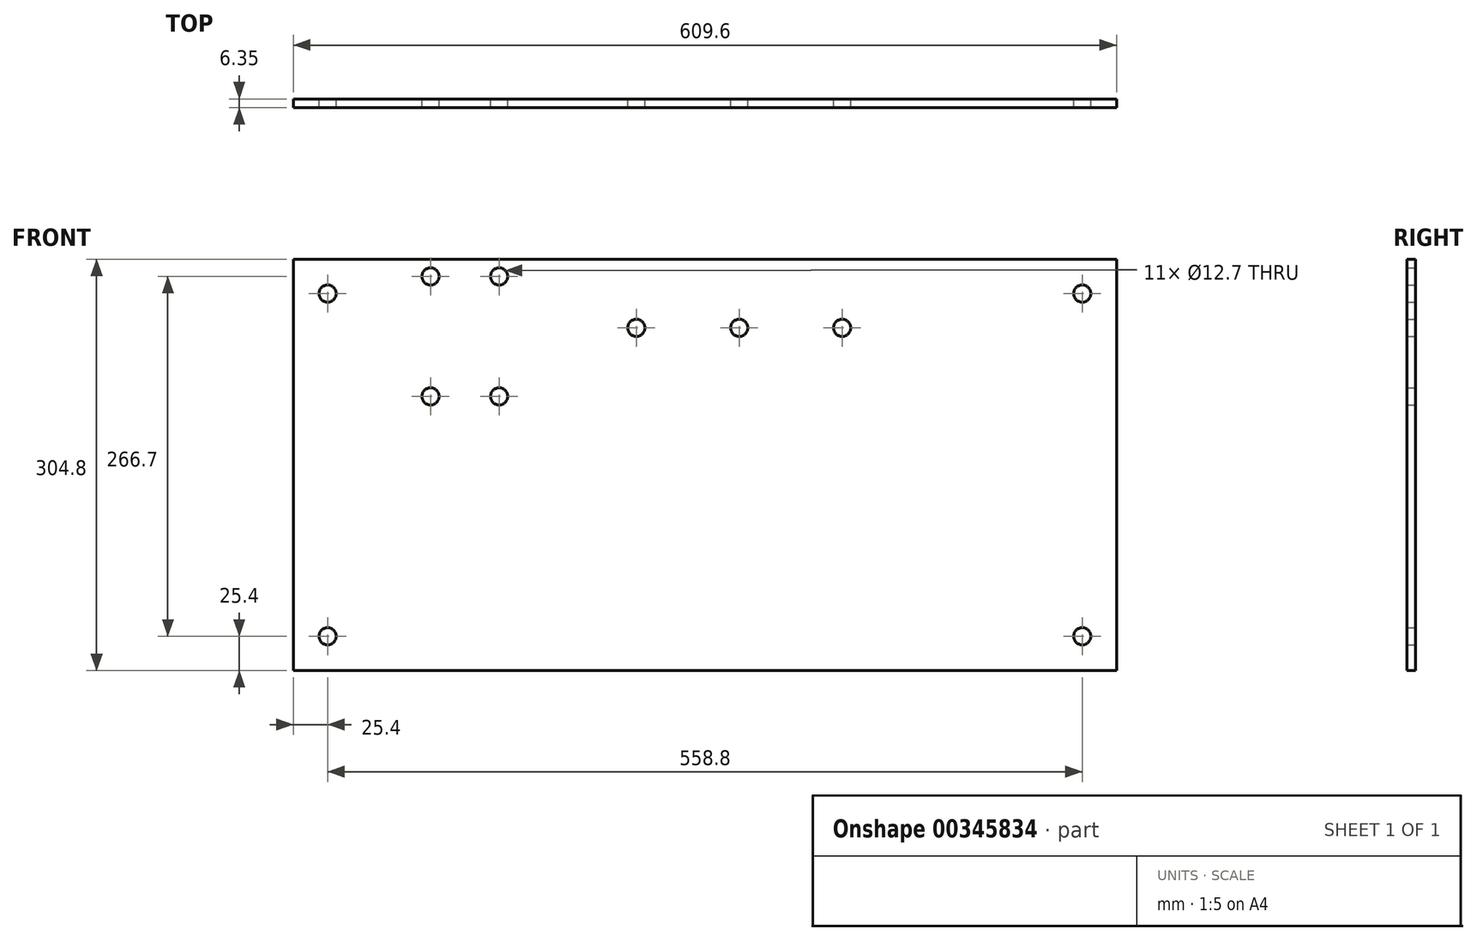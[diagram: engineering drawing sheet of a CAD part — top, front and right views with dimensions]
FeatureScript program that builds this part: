
annotation { "Feature Type Name" : "Feature", "Feature Type Description" : "" }
export const myFeature = defineFeature(function(context is Context, id is Id, definition is map)
    precondition{}
    {
        {
            var Q0;
            Q0=qCreatedBy(makeId("Front.planeOp"),FACE);
            var sketch = newSketch(context, id + "F0", { "sketchPlane" : qUnion([Q0])});
            skLineSegment(sketch, "E0.bottom", {"start": v(304.8, -152.4) * mm, "end": v(-304.8, -152.4) * mm});
            skLineSegment(sketch, "E0.top", {"start": v(304.8, 152.4) * mm, "end": v(-304.8, 152.4) * mm});
            skLineSegment(sketch, "E0.left", {"start": v(304.8, -152.4) * mm, "end": v(304.8, 152.4) * mm});
            skLineSegment(sketch, "E0.right", {"start": v(-304.8, -152.4) * mm, "end": v(-304.8, 152.4) * mm});
            skPoint(sketch, "E0.middle", {"position": v(0, 0) * mm});
            skPoint(sketch, "E1", {"position": v(101.6, 101.6) * mm});
            skPoint(sketch, "E2", {"position": v(25.4, 101.6) * mm});
            skPoint(sketch, "E3", {"position": v(0, 132.43) * mm});
            skPoint(sketch, "E4", {"position": v(-50.8, 101.6) * mm});
            skPoint(sketch, "E5", {"position": v(-279.4, 127) * mm});
            skPoint(sketch, "E6", {"position": v(279.4, 127) * mm});
            skPoint(sketch, "E7", {"position": v(279.4, -127) * mm});
            skPoint(sketch, "E8", {"position": v(-279.4, -127) * mm});
            skPoint(sketch, "E9", {"position": v(-203.2, 139.7) * mm});
            skPoint(sketch, "E10", {"position": v(-152.4, 139.7) * mm});
            skPoint(sketch, "E11", {"position": v(-203.2, 50.8) * mm});
            skPoint(sketch, "E12", {"position": v(-152.4, 50.8) * mm});
            skSolve(sketch);
        }
        {
            var Q0;
            Q0=makeQuery(id+"F0.imprint","IMPRINT",FACE,{"disambiguationData":[TD([[makeQuery(id+"F0.imprint","IMPRINT",EDGE,{"derivedFrom":sQuery(id+"F0.wireOp",EDGE,"E0.bottom")}),-1.0]])]});
            extrude(context, id + "F2", {"entities" : qUnion([Q0]), "depth" : 6.35 * mm});
        }
        {
            var Q0;
            Q0=sQuery(id+"F0.wireOp",VERTEX,"E1");
            var Q1;
            Q1=sQuery(id+"F0.wireOp",VERTEX,"E2");
            var Q2;
            Q2=sQuery(id+"F0.wireOp",VERTEX,"E4");
            var Q3;
            Q3=sQuery(id+"F0.wireOp",VERTEX,"E8");
            var Q4;
            Q4=sQuery(id+"F0.wireOp",VERTEX,"E5");
            var Q5;
            Q5=sQuery(id+"F0.wireOp",VERTEX,"E7");
            var Q6;
            Q6=sQuery(id+"F0.wireOp",VERTEX,"E6");
            var Q7;
            Q7=sQuery(id+"F0.wireOp",VERTEX,"E11");
            var Q8;
            Q8=sQuery(id+"F0.wireOp",VERTEX,"E12");
            var Q9;
            Q9=sQuery(id+"F0.wireOp",VERTEX,"E10");
            var Q10;
            Q10=sQuery(id+"F0.wireOp",VERTEX,"E9");
            var Q11;
            Q11=makeQuery(id+"F2.opExtrude","SWEPT_BODY",BODY,{"disambiguationData":[OSD([sQuery(id+"F0.wireOp",EDGE,"E0.bottom"),sQuery(id+"F0.wireOp",EDGE,"E0.top"),sQuery(id+"F0.wireOp",EDGE,"E0.left"),sQuery(id+"F0.wireOp",EDGE,"E0.right")])]});
            hole(context, id + "F1", {"style" : HoleStyle.SIMPLE, "endStyle" : HoleEndStyle.THROUGH, "oppositeDirection" : true, "holeDiameter" : 12.7 * mm, "locations" : qUnion([Q0, Q1, Q2, Q3, Q4, Q5, Q6, Q7, Q8, Q9, Q10]), "scope" : qUnion([Q11]), "isTappedThrough" : true});
        }
    });
